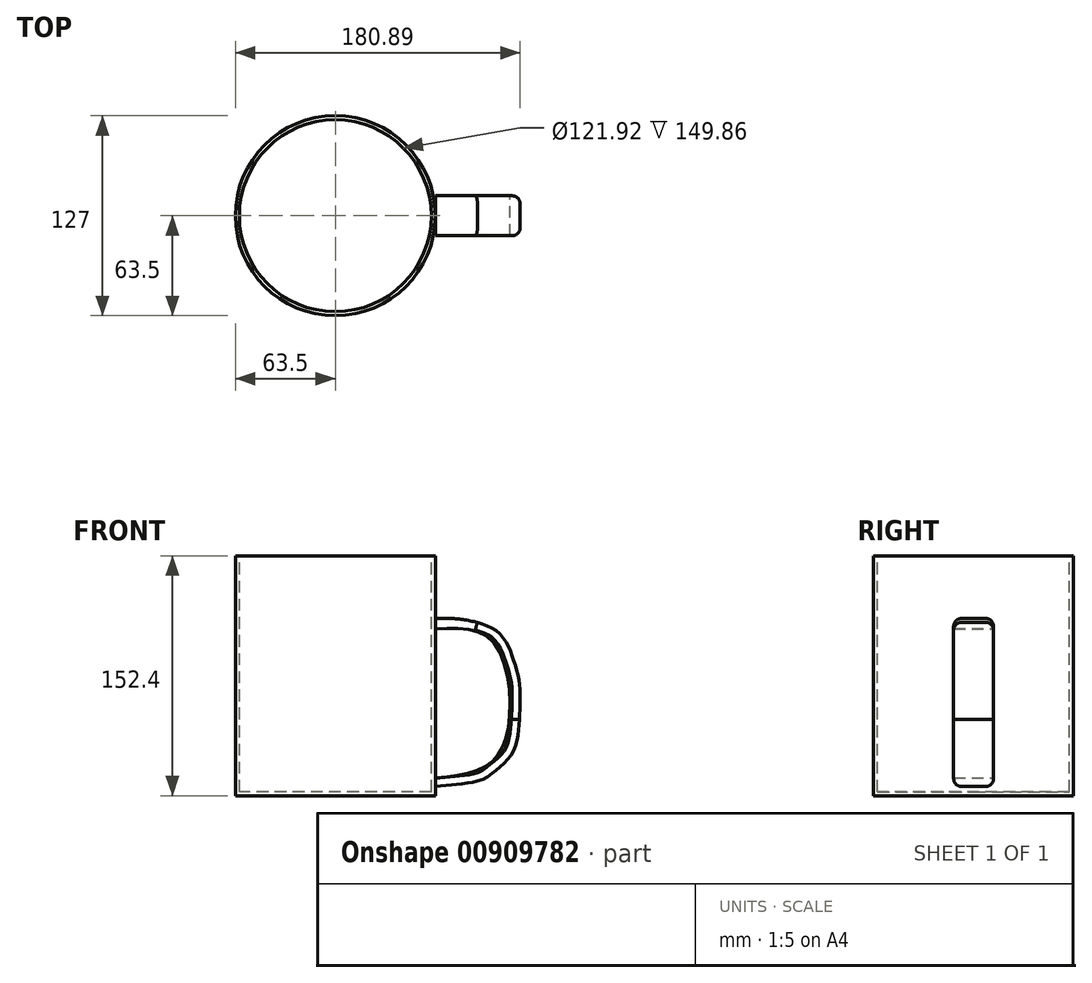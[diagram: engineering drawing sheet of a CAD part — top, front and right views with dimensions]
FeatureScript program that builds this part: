
annotation { "Feature Type Name" : "Feature", "Feature Type Description" : "" }
export const myFeature = defineFeature(function(context is Context, id is Id, definition is map)
    precondition{}
    {
        {
            var Q0;
            Q0=qCreatedBy(makeId("Front.planeOp"),FACE);
            var sketch = newSketch(context, id + "F0", { "sketchPlane" : qUnion([Q0])});
            skLineSegment(sketch, "E0.bottom", {"start": v(0, 0) * mm, "end": v(-63.5, 0) * mm});
            skLineSegment(sketch, "E0.top", {"start": v(0, -152.4) * mm, "end": v(-63.5, -152.4) * mm});
            skLineSegment(sketch, "E0.left", {"start": v(0, 0) * mm, "end": v(0, -152.4) * mm});
            skLineSegment(sketch, "E0.right", {"start": v(-63.5, 0) * mm, "end": v(-63.5, -152.4) * mm});
            skSolve(sketch);
        }
        {
            var Q0;
            Q0 = qSketchRegion(id + "F0", true);
            var Q1;
            Q1=sQuery(id+"F0.wireOp",EDGE,"E0.left");
            revolve(context, id + "F1", {"surfaceOperationType" : NewSurfaceOperationType.NEW, "entities" : qUnion([Q0]), "axis" : qUnion([Q1]), "revolveType" : RevolveType.FULL});
        }
        {
            var Q0;
            Q0=makeQuery(id+"F1.opRevolve","SWEPT_FACE",FACE,{"disambiguationData":[OSD([sQuery(id+"F0.wireOp",EDGE,"E0.bottom")])]});
            shell(context, id + "F2", {"entities" : qUnion([Q0]), "thickness" : 2.54 * mm});
        }
        {
            var Q0;
            Q0=qCreatedBy(makeId("Front.planeOp"),FACE);
            var sketch = newSketch(context, id + "F3", { "sketchPlane" : qUnion([Q0])});
            skFitSpline(sketch, "E1", {"points": [v(63.61, -46.51) * mm, v(99.04, -53.44) * mm, v(110.59, -104.01) * mm, v(97.5, -132.5) * mm, v(64.05, -141.06) * mm], "startDerivative": vector(166.1, 9.26) * mm, "endDerivative": vector(-158.6, -17.18) * mm});
            skLineSegment(sketch, "E2", {"start": v(64.05, -141.06) * mm, "end": v(63.55, -141.06) * mm});
            skLineSegment(sketch, "E3", {"start": v(63.55, -141.06) * mm, "end": v(63.55, -141.94) * mm});
            skLineSegment(sketch, "E4", {"start": v(63.55, -141.94) * mm, "end": v(63.55, -142.7) * mm});
            skLineSegment(sketch, "E5", {"start": v(63.55, -142.7) * mm, "end": v(63.55, -146.54) * mm});
            skFitSpline(sketch, "E6", {"points": [v(63.55, -146.54) * mm, v(77.4, -145.14) * mm, v(92.95, -142.23) * mm, v(101.8, -136.4) * mm, v(112.7, -124.74) * mm, v(117.01, -104.02) * mm], "startDerivative": vector(69.68, 6.8) * mm, "endDerivative": vector(7.8, 95.54) * mm});
            skFitSpline(sketch, "E7", {"points": [v(117.01, -104.02) * mm, v(117.01, -81.66) * mm, v(113.74, -67.77) * mm, v(104.9, -49.91) * mm, v(90.24, -42.28) * mm], "startDerivative": vector(3.48, 86.92) * mm, "endDerivative": vector(-67.37, 21.98) * mm});
            skFitSpline(sketch, "E8", {"points": [v(90.24, -42.28) * mm, v(77.56, -40.08) * mm, v(63.55, -39.95) * mm], "startDerivative": vector(-25.54, 5.54) * mm, "endDerivative": vector(-27.82, -0.83) * mm});
            skLineSegment(sketch, "E9", {"start": v(63.55, -39.95) * mm, "end": v(63.61, -46.51) * mm});
            skSolve(sketch);
        }
        {
            var Q0;
            Q0 = qSketchRegion(id + "F3", true);
            extrude(context, id + "F4", {"entities" : qUnion([Q0]), "endBound" : BoundingType.SYMMETRIC, "depth" : 25.4 * mm, "offsetDistance" : 25.4 * mm});
        }
        {
            var Q0;
            Q0=makeQuery(id+"F4.opExtrude","CAP_EDGE",EDGE,{"disambiguationData":[OSD([sQuery(id+"F3.wireOp",EDGE,"E8")])],"isStart":false});
            var Q1;
            Q1=makeQuery(id+"F4.opExtrude","CAP_EDGE",EDGE,{"disambiguationData":[OSD([sQuery(id+"F3.wireOp",EDGE,"E7")])],"isStart":false});
            var Q2;
            Q2=makeQuery(id+"F4.opExtrude","CAP_EDGE",EDGE,{"disambiguationData":[OSD([sQuery(id+"F3.wireOp",EDGE,"E6")])],"isStart":false});
            var Q3;
            Q3=makeQuery(id+"F4.opExtrude","CAP_EDGE",EDGE,{"disambiguationData":[OSD([sQuery(id+"F3.wireOp",EDGE,"E6")])],"isStart":true});
            var Q4;
            Q4=makeQuery(id+"F4.opExtrude","CAP_EDGE",EDGE,{"disambiguationData":[OSD([sQuery(id+"F3.wireOp",EDGE,"E7")])],"isStart":true});
            var Q5;
            Q5=makeQuery(id+"F4.opExtrude","CAP_EDGE",EDGE,{"disambiguationData":[OSD([sQuery(id+"F3.wireOp",EDGE,"E8")])],"isStart":true});
            fillet(context, id + "F5", {"entities" : qUnion([Q0, Q1, Q2, Q3, Q4, Q5]), "radius" : 5.08 * mm, "tangentPropagation" : true, "allowEdgeOverflow" : false});
        }
    });
